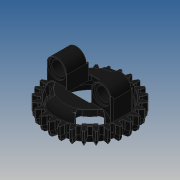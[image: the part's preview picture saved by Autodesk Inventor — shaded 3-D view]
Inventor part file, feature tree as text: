
AUTODESK INVENTOR PART (.ipt)
format: ipt  version: 2022.2 (Build 262287000, 287)  size: 13,010,944 bytes
history: native  units: in
note: dims shown in document units (in); Inventor stores cm internally (conversion verified against a paired STEP export)
features: sketch x14, extrude x9, revolve x4, fillet x3, projected_geometry x3, plane x2, pattern_circular x2, loft x2, surface_op x2, draft x1, mirror x1, other x1
ambient origin geometry x8: Origin, YZ Plane, XZ Plane, XY Plane, X Axis, Y Axis, Z Axis, Center Point
bodies: Solid1 (feature_tree)
feature tree (44):
  sketch  "Sketch2"  dims[d0=0.1102in d1=0.1102in]
  revolve  "Revolution1"  [1 undecoded]
  extrude  "Extrusion1"  Depth=0.0236in
  draft  "FaceDraft1"
  fillet  "Fillet1"  Radius=0.0945in
  plane  "Work Plane3"
  revolve  "Revolution2"  [1 undecoded]
  revolve  "Revolution3"  Angle=90.0deg
  pattern_circular  "Circular Pattern1"  [2 undecoded]
  sketch  "Sketch7"  dims[d7=0.8504in d8=90.0deg]
  extrude  "Extrusion2"  Depth=0.0039in
  sketch  "Sketch8"  dims[d9=0.063in]
  extrude  "Extrusion3"  Depth=0.0039in
  extrude  "Extrusion4"  Depth=0.0039in
  extrude  "Extrusion5"  TaperAngle=90.0deg  [1 undecoded]
  revolve  "Revolution4"  [1 undecoded]
  extrude  "Extrusion6"  Depth=0.0039in
  extrude  "Extrusion7"  Depth=0.0039in
  extrude  "Extrusion8"  Depth=0.0039in
  extrude  "Extrusion9"  Depth=0.0039in
  sketch  "Sketch13"  dims[d16=0.3037in]
  plane  "Work Plane4"
  sketch  "Sketch14"  dims[d18=0.3937in d19=0.0in]
  sketch  "Sketch15"  dims[d20=0.0472in d21=0.3481in d22=0.063in d23=0.1821in d24=0.063in d25=90.0deg d26=-0.3092in d27=0.1732in d28=0.0102in d29=0.8078in d30=0.8504in d31=22.5deg d32=1.5748in d33=360.0deg d35=0.3465in d36=0.0157in d37=0.2734in d38=0.4409in d39=0.3937in d40=0.0in d41=0.1575in d42=0.189in d43=0.2835in d44=0.6299in d45=0.3937in d46=0.0in d47=0.315in d48=0.0in d49=0.315in d50=0.0in d51=22.5deg d52=0.0787in d53=0.0in d54=0.252in d55=0.0315in d56=0.0in d58=0.252in d59=0.0315in d60=0.0in d61=0.0648in d62=0.0858in d63=0.0567in d64=0.0269in d65=0.0315in d66=0.0in d67=0.0674in d68=0.0324in d69=0.0081in d72=0.0315in d73=0.063in d74=0.0in d111=0.0in d112=90.0deg d113=0.0in d114=90.0deg d115=0.0in d116=90.0deg d117=0.0in d118=90.0deg d119=0.0in d120=90.0deg d121=0.0in d122=90.0deg d123=0.0in d124=90.0deg d125=0.0in d126=90.0deg d127=0.0in d128=90.0deg d129=0.0in d130=90.0deg d131=0.0in d132=90.0deg d133=0.0in d134=90.0deg d135=0.0in d136=90.0deg d137=0.0in d138=90.0deg d139=0.0in d140=90.0deg d141=0.0in d142=90.0deg d143=0.0in d144=90.0deg d145=0.1969in d146=0.1969in d147=0.1969in d148=0.0in d149=0.0039in d150=11.0236in d151=360.0deg d153=0.0039in]
  sketch  "3D Sketch2"
  sketch  "3D Sketch1"
  loft  "Loft3"
  loft  "Loft4"
  surface_op  "Sculpt1"
  mirror  "Mirror1"
  fillet  "Fillet2"  Radius=0.3465in
  pattern_circular  "Circular Pattern2"  [2 undecoded]
  fillet  "Fillet3"  Radius=0.2734in
  sketch  "Sketch3"  dims[d2=0.9921in d3=0.0236in d4=0.0945in]
  sketch  "Sketch6"  dims[d5=0.9449in d6=0.063in]
  sketch  "Sketch9"  dims[d10=0.9134in]
  projected_geometry  "Projected Loop1"
  projected_geometry  "Projected Loop2"
  projected_geometry  "Projected Loop3"
  sketch  "Sketch10"  dims[d11=0.0787in]
  sketch  "Sketch11"  dims[d12=0.6796in]
  sketch  "Sketch12"  dims[d13=45.0deg]
  other  "Srf3"
  surface_op  "Boundary Patch2"
note: 8 required parameter values undecoded (feature->parameter linkage not recoverable at this tier; creation-order binding heuristic only, values carry confidence <= 0.55)